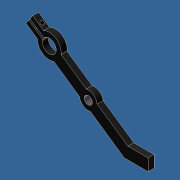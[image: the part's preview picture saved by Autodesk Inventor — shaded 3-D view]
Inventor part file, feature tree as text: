
AUTODESK INVENTOR PART (.ipt)
format: ipt  version: unknown  size: 235,520 bytes
history: native  units: in
note: dims shown in document units (in); Inventor stores cm internally (conversion verified against a paired STEP export)
features: sketch x7, extrude x5, hole x2
ambient origin geometry x8: Origin, YZ Plane, XZ Plane, XY Plane, X Axis, Y Axis, Z Axis, Center Point
bodies: Solid1 (feature_tree)
feature tree (14):
  extrude  "Extrusion1"  Depth=0.5in
  extrude  "Extrusion2"  Depth=1.0in
  extrude  "Extrusion3"  Depth=0.25in TaperAngle=0.0deg
  extrude  "Extrusion4"  Depth=1.0in
  hole  "Hole1"  [1 undecoded]
  hole  "Hole2"  [1 undecoded]
  extrude  "Extrusion5"  Depth=0.25in TaperAngle=0.0deg
  sketch  "Sketch1"  dims[d3=0.5in d4=0.5in]
  sketch  "Sketch2"  dims[d5=0.9998in d6=1.0in]
  sketch  "Sketch3"  dims[d7=5.0in d8=0.25in d9=0.0in]
  sketch  "Sketch4"  dims[d10=1.0in d11=1.0in]
  sketch  "Sketch5"  dims[d12=0.25in d13=0.0in d14=0.581in]
  sketch  "Sketch6"  dims[d15=0.25in d16=0.0in d17=0.05in]
  sketch  "Sketch7"  dims[d18=0.05in d19=0.25in d20=0.0in d21=0.25in d22=0.125in d23=0.15in d24=0.75in d25=0.385in d26=0.25in d27=0.5635in d28=1.0in d29=0.8108in d30=0.25in d31=2.0in d32=0.341in d33=0.75in d34=0.385in d35=0.25in d36=0.5635in d37=1.0in d38=0.8108in d39=0.75in d40=0.25in d41=0.0in]
note: 2 required parameter values undecoded (feature->parameter linkage not recoverable at this tier; creation-order binding heuristic only, values carry confidence <= 0.55)
